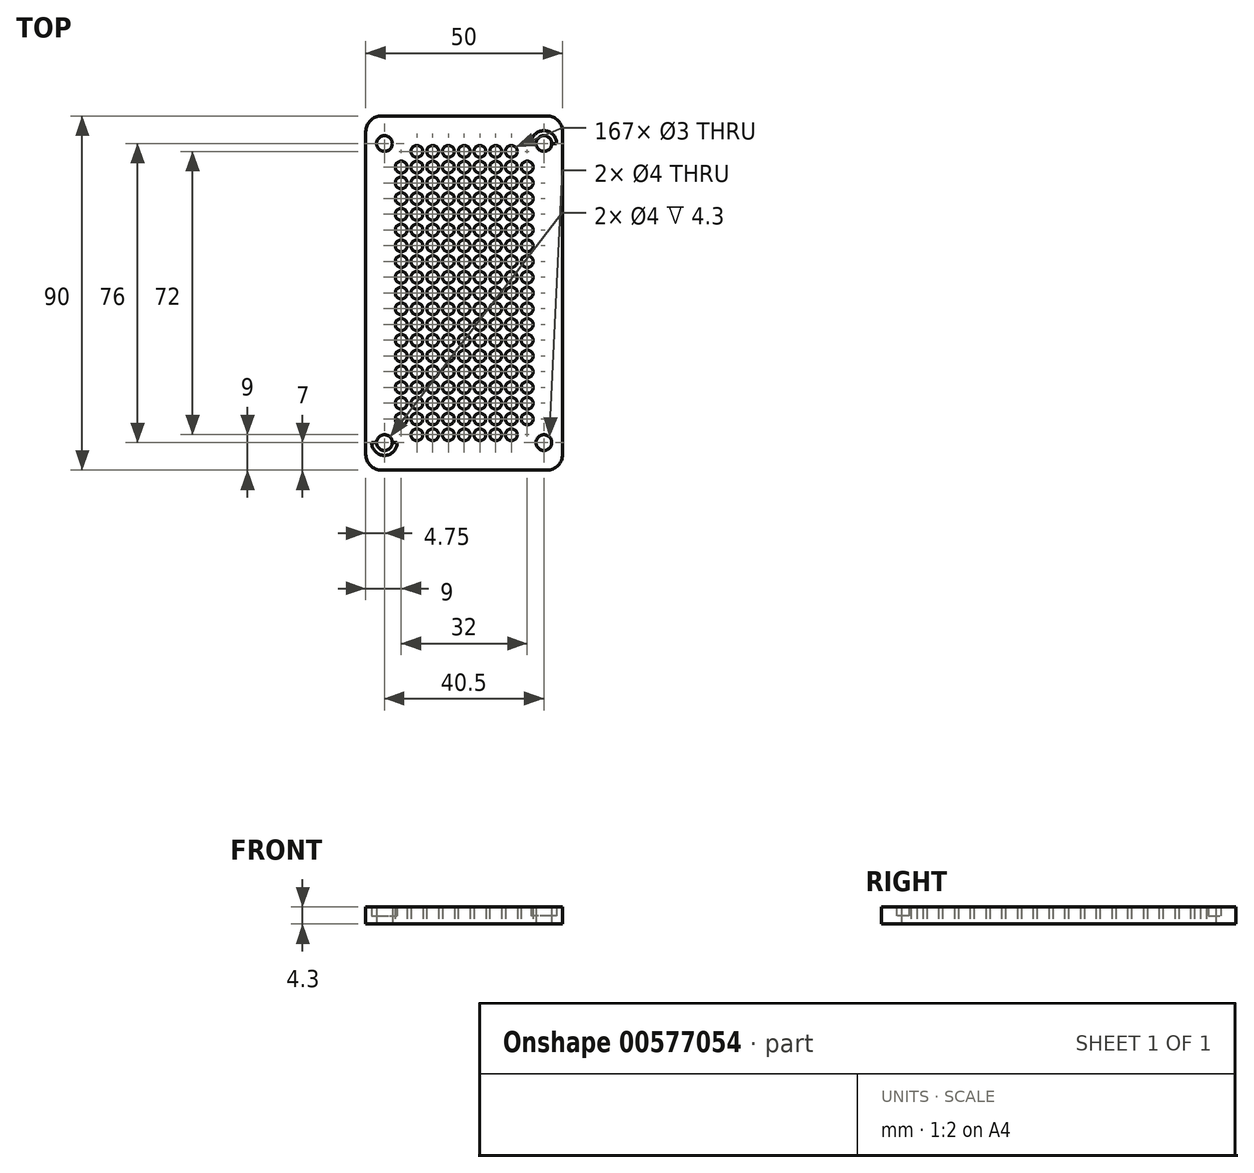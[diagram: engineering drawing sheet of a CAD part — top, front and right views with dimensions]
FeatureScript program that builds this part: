
annotation { "Feature Type Name" : "Feature", "Feature Type Description" : "" }
export const myFeature = defineFeature(function(context is Context, id is Id, definition is map)
    precondition{}
    {
        {
            var Q0;
            Q0=qCreatedBy(makeId("Top.planeOp"),FACE);
            var sketch = newSketch(context, id + "F0", { "sketchPlane" : qUnion([Q0])});
            skLineSegment(sketch, "E0.bottom", {"start": v(21, -45) * mm, "end": v(-21, -45) * mm});
            skLineSegment(sketch, "E0.top", {"start": v(21, 45) * mm, "end": v(-21, 45) * mm});
            skLineSegment(sketch, "E0.left", {"start": v(25, -41) * mm, "end": v(25, 41) * mm});
            skLineSegment(sketch, "E0.right", {"start": v(-25, -41) * mm, "end": v(-25, 41) * mm});
            skPoint(sketch, "E0.middle", {"position": v(0, 0) * mm});
            skCircle(sketch, "E1", {"center": v(0, 0) * mm, "radius": 1.5 * mm});
            skCircle(sketch, "E2.0.1.0", {"center": v(0, 4) * mm, "radius": 1.5 * mm});
            skCircle(sketch, "E2.0.2.0", {"center": v(0, 8) * mm, "radius": 1.5 * mm});
            skCircle(sketch, "E2.0.3.0", {"center": v(0, 12) * mm, "radius": 1.5 * mm});
            skCircle(sketch, "E2.0.4.0", {"center": v(0, 16) * mm, "radius": 1.5 * mm});
            skCircle(sketch, "E2.0.5.0", {"center": v(0, 20) * mm, "radius": 1.5 * mm});
            skCircle(sketch, "E2.0.6.0", {"center": v(0, 24) * mm, "radius": 1.5 * mm});
            skCircle(sketch, "E2.0.7.0", {"center": v(0, 28) * mm, "radius": 1.5 * mm});
            skCircle(sketch, "E2.0.8.0", {"center": v(0, 32) * mm, "radius": 1.5 * mm});
            skCircle(sketch, "E2.0.9.0", {"center": v(0, 36) * mm, "radius": 1.5 * mm});
            skCircle(sketch, "E2.1.0.0", {"center": v(4, 0) * mm, "radius": 1.5 * mm});
            skCircle(sketch, "E2.1.1.0", {"center": v(4, 4) * mm, "radius": 1.5 * mm});
            skCircle(sketch, "E2.1.2.0", {"center": v(4, 8) * mm, "radius": 1.5 * mm});
            skCircle(sketch, "E2.1.3.0", {"center": v(4, 12) * mm, "radius": 1.5 * mm});
            skCircle(sketch, "E2.1.4.0", {"center": v(4, 16) * mm, "radius": 1.5 * mm});
            skCircle(sketch, "E2.1.5.0", {"center": v(4, 20) * mm, "radius": 1.5 * mm});
            skCircle(sketch, "E2.1.6.0", {"center": v(4, 24) * mm, "radius": 1.5 * mm});
            skCircle(sketch, "E2.1.7.0", {"center": v(4, 28) * mm, "radius": 1.5 * mm});
            skCircle(sketch, "E2.1.8.0", {"center": v(4, 32) * mm, "radius": 1.5 * mm});
            skCircle(sketch, "E2.1.9.0", {"center": v(4, 36) * mm, "radius": 1.5 * mm});
            skCircle(sketch, "E2.2.0.0", {"center": v(8, 0) * mm, "radius": 1.5 * mm});
            skCircle(sketch, "E2.2.1.0", {"center": v(8, 4) * mm, "radius": 1.5 * mm});
            skCircle(sketch, "E2.2.2.0", {"center": v(8, 8) * mm, "radius": 1.5 * mm});
            skCircle(sketch, "E2.2.3.0", {"center": v(8, 12) * mm, "radius": 1.5 * mm});
            skCircle(sketch, "E2.2.4.0", {"center": v(8, 16) * mm, "radius": 1.5 * mm});
            skCircle(sketch, "E2.2.5.0", {"center": v(8, 20) * mm, "radius": 1.5 * mm});
            skCircle(sketch, "E2.2.6.0", {"center": v(8, 24) * mm, "radius": 1.5 * mm});
            skCircle(sketch, "E2.2.7.0", {"center": v(8, 28) * mm, "radius": 1.5 * mm});
            skCircle(sketch, "E2.2.8.0", {"center": v(8, 32) * mm, "radius": 1.5 * mm});
            skCircle(sketch, "E2.2.9.0", {"center": v(8, 36) * mm, "radius": 1.5 * mm});
            skCircle(sketch, "E2.3.0.0", {"center": v(12, 0) * mm, "radius": 1.5 * mm});
            skCircle(sketch, "E2.3.1.0", {"center": v(12, 4) * mm, "radius": 1.5 * mm});
            skCircle(sketch, "E2.3.2.0", {"center": v(12, 8) * mm, "radius": 1.5 * mm});
            skCircle(sketch, "E2.3.3.0", {"center": v(12, 12) * mm, "radius": 1.5 * mm});
            skCircle(sketch, "E2.3.4.0", {"center": v(12, 16) * mm, "radius": 1.5 * mm});
            skCircle(sketch, "E2.3.5.0", {"center": v(12, 20) * mm, "radius": 1.5 * mm});
            skCircle(sketch, "E2.3.6.0", {"center": v(12, 24) * mm, "radius": 1.5 * mm});
            skCircle(sketch, "E2.3.7.0", {"center": v(12, 28) * mm, "radius": 1.5 * mm});
            skCircle(sketch, "E2.3.8.0", {"center": v(12, 32) * mm, "radius": 1.5 * mm});
            skCircle(sketch, "E2.3.9.0", {"center": v(12, 36) * mm, "radius": 1.5 * mm});
            skCircle(sketch, "E2.4.0.0", {"center": v(16, 0) * mm, "radius": 1.5 * mm});
            skCircle(sketch, "E2.4.1.0", {"center": v(16, 4) * mm, "radius": 1.5 * mm});
            skCircle(sketch, "E2.4.2.0", {"center": v(16, 8) * mm, "radius": 1.5 * mm});
            skCircle(sketch, "E2.4.3.0", {"center": v(16, 12) * mm, "radius": 1.5 * mm});
            skCircle(sketch, "E2.4.4.0", {"center": v(16, 16) * mm, "radius": 1.5 * mm});
            skCircle(sketch, "E2.4.5.0", {"center": v(16, 20) * mm, "radius": 1.5 * mm});
            skCircle(sketch, "E2.4.6.0", {"center": v(16, 24) * mm, "radius": 1.5 * mm});
            skCircle(sketch, "E2.4.7.0", {"center": v(16, 28) * mm, "radius": 1.5 * mm});
            skCircle(sketch, "E2.4.8.0", {"center": v(16, 32) * mm, "radius": 1.5 * mm});
            skLineSegment(sketch, "E2.direction1", {"start": v(0, 0) * mm, "end": v(4, 0) * mm, "construction": true});
            skLineSegment(sketch, "E2.direction2", {"start": v(0, 0) * mm, "end": v(0, 4) * mm, "construction": true});
            skCircle(sketch, "E3.MirrorC", {"center": v(-12, 0) * mm, "radius": 1.5 * mm});
            skCircle(sketch, "E4.MirrorC", {"center": v(-16, 24) * mm, "radius": 1.5 * mm});
            skCircle(sketch, "E5.MirrorC", {"center": v(-8, 28) * mm, "radius": 1.5 * mm});
            skCircle(sketch, "E6.MirrorC", {"center": v(-12, 16) * mm, "radius": 1.5 * mm});
            skCircle(sketch, "E7.MirrorC", {"center": v(-16, 12) * mm, "radius": 1.5 * mm});
            skCircle(sketch, "E8.MirrorC", {"center": v(-8, 4) * mm, "radius": 1.5 * mm});
            skCircle(sketch, "E9.MirrorC", {"center": v(-12, 28) * mm, "radius": 1.5 * mm});
            skCircle(sketch, "E10.MirrorC", {"center": v(-8, 36) * mm, "radius": 1.5 * mm});
            skCircle(sketch, "E11.MirrorC", {"center": v(-16, 20) * mm, "radius": 1.5 * mm});
            skCircle(sketch, "E12.MirrorC", {"center": v(-8, 24) * mm, "radius": 1.5 * mm});
            skCircle(sketch, "E13.MirrorC", {"center": v(-12, 12) * mm, "radius": 1.5 * mm});
            skCircle(sketch, "E14.MirrorC", {"center": v(-16, 8) * mm, "radius": 1.5 * mm});
            skCircle(sketch, "E15.MirrorC", {"center": v(-8, 0) * mm, "radius": 1.5 * mm});
            skCircle(sketch, "E16.MirrorC", {"center": v(-12, 24) * mm, "radius": 1.5 * mm});
            skCircle(sketch, "E17.MirrorC", {"center": v(-8, 16) * mm, "radius": 1.5 * mm});
            skCircle(sketch, "E18.MirrorC", {"center": v(-16, 0) * mm, "radius": 1.5 * mm});
            skCircle(sketch, "E19.MirrorC", {"center": v(-8, 32) * mm, "radius": 1.5 * mm});
            skCircle(sketch, "E20.MirrorC", {"center": v(-16, 16) * mm, "radius": 1.5 * mm});
            skCircle(sketch, "E21.MirrorC", {"center": v(-12, 8) * mm, "radius": 1.5 * mm});
            skCircle(sketch, "E22.MirrorC", {"center": v(-8, 20) * mm, "radius": 1.5 * mm});
            skCircle(sketch, "E23.MirrorC", {"center": v(-16, 32) * mm, "radius": 1.5 * mm});
            skCircle(sketch, "E24.MirrorC", {"center": v(-16, 4) * mm, "radius": 1.5 * mm});
            skCircle(sketch, "E25.MirrorC", {"center": v(-12, 20) * mm, "radius": 1.5 * mm});
            skCircle(sketch, "E26.MirrorC", {"center": v(-8, 12) * mm, "radius": 1.5 * mm});
            skCircle(sketch, "E27.MirrorC", {"center": v(-12, 36) * mm, "radius": 1.5 * mm});
            skCircle(sketch, "E28.MirrorC", {"center": v(-12, 4) * mm, "radius": 1.5 * mm});
            skCircle(sketch, "E29.MirrorC", {"center": v(-16, 28) * mm, "radius": 1.5 * mm});
            skCircle(sketch, "E30.MirrorC", {"center": v(-8, 8) * mm, "radius": 1.5 * mm});
            skCircle(sketch, "E31.MirrorC", {"center": v(-12, 32) * mm, "radius": 1.5 * mm});
            skCircle(sketch, "E32.MirrorC", {"center": v(-4, 16) * mm, "radius": 1.5 * mm});
            skCircle(sketch, "E33.MirrorC", {"center": v(-4, 12) * mm, "radius": 1.5 * mm});
            skCircle(sketch, "E34.MirrorC", {"center": v(-4, 8) * mm, "radius": 1.5 * mm});
            skCircle(sketch, "E35.MirrorC", {"center": v(-4, 36) * mm, "radius": 1.5 * mm});
            skCircle(sketch, "E36.MirrorC", {"center": v(-4, 20) * mm, "radius": 1.5 * mm});
            skCircle(sketch, "E37.MirrorC", {"center": v(-4, 32) * mm, "radius": 1.5 * mm});
            skCircle(sketch, "E38.MirrorC", {"center": v(-4, 0) * mm, "radius": 1.5 * mm});
            skCircle(sketch, "E39.MirrorC", {"center": v(-4, 4) * mm, "radius": 1.5 * mm});
            skCircle(sketch, "E40.MirrorC", {"center": v(-4, 24) * mm, "radius": 1.5 * mm});
            skCircle(sketch, "E41.MirrorC", {"center": v(-4, 28) * mm, "radius": 1.5 * mm});
            skCircle(sketch, "E42.MirrorC", {"center": v(16, -24) * mm, "radius": 1.5 * mm});
            skCircle(sketch, "E43.MirrorC", {"center": v(-12, -12) * mm, "radius": 1.5 * mm});
            skCircle(sketch, "E44.MirrorC", {"center": v(-12, -4) * mm, "radius": 1.5 * mm});
            skCircle(sketch, "E45.MirrorC", {"center": v(4, -16) * mm, "radius": 1.5 * mm});
            skCircle(sketch, "E46.MirrorC", {"center": v(-8, -32) * mm, "radius": 1.5 * mm});
            skCircle(sketch, "E47.MirrorC", {"center": v(-4, -36) * mm, "radius": 1.5 * mm});
            skCircle(sketch, "E48.MirrorC", {"center": v(8, -4) * mm, "radius": 1.5 * mm});
            skCircle(sketch, "E49.MirrorC", {"center": v(12, -28) * mm, "radius": 1.5 * mm});
            skCircle(sketch, "E50.MirrorC", {"center": v(-16, -24) * mm, "radius": 1.5 * mm});
            skCircle(sketch, "E51.MirrorC", {"center": v(-8, -28) * mm, "radius": 1.5 * mm});
            skCircle(sketch, "E52.MirrorC", {"center": v(12, -32) * mm, "radius": 1.5 * mm});
            skCircle(sketch, "E53.MirrorC", {"center": v(8, -8) * mm, "radius": 1.5 * mm});
            skCircle(sketch, "E54.MirrorC", {"center": v(-4, -20) * mm, "radius": 1.5 * mm});
            skCircle(sketch, "E55.MirrorC", {"center": v(-16, -16) * mm, "radius": 1.5 * mm});
            skCircle(sketch, "E56.MirrorC", {"center": v(4, -20) * mm, "radius": 1.5 * mm});
            skCircle(sketch, "E57.MirrorC", {"center": v(-16, -28) * mm, "radius": 1.5 * mm});
            skCircle(sketch, "E58.MirrorC", {"center": v(16, -28) * mm, "radius": 1.5 * mm});
            skCircle(sketch, "E59.MirrorC", {"center": v(12, -4) * mm, "radius": 1.5 * mm});
            skCircle(sketch, "E60.MirrorC", {"center": v(-12, -16) * mm, "radius": 1.5 * mm});
            skCircle(sketch, "E61.MirrorC", {"center": v(12, -36) * mm, "radius": 1.5 * mm});
            skCircle(sketch, "E62.MirrorC", {"center": v(8, -12) * mm, "radius": 1.5 * mm});
            skCircle(sketch, "E63.MirrorC", {"center": v(-4, -32) * mm, "radius": 1.5 * mm});
            skCircle(sketch, "E64.MirrorC", {"center": v(-12, -8) * mm, "radius": 1.5 * mm});
            skCircle(sketch, "E65.MirrorC", {"center": v(4, -24) * mm, "radius": 1.5 * mm});
            skCircle(sketch, "E66.MirrorC", {"center": v(-8, -8) * mm, "radius": 1.5 * mm});
            skCircle(sketch, "E67.MirrorC", {"center": v(-8, -4) * mm, "radius": 1.5 * mm});
            skCircle(sketch, "E68.MirrorC", {"center": v(-16, -32) * mm, "radius": 1.5 * mm});
            skCircle(sketch, "E69.MirrorC", {"center": v(-16, -8) * mm, "radius": 1.5 * mm});
            skCircle(sketch, "E70.MirrorC", {"center": v(16, -4) * mm, "radius": 1.5 * mm});
            skCircle(sketch, "E71.MirrorC", {"center": v(12, -8) * mm, "radius": 1.5 * mm});
            skCircle(sketch, "E72.MirrorC", {"center": v(16, -32) * mm, "radius": 1.5 * mm});
            skCircle(sketch, "E73.MirrorC", {"center": v(8, -20) * mm, "radius": 1.5 * mm});
            skCircle(sketch, "E74.MirrorC", {"center": v(-4, -4) * mm, "radius": 1.5 * mm});
            skCircle(sketch, "E75.MirrorC", {"center": v(8, -36) * mm, "radius": 1.5 * mm});
            skCircle(sketch, "E76.MirrorC", {"center": v(16, -20) * mm, "radius": 1.5 * mm});
            skCircle(sketch, "E77.MirrorC", {"center": v(-8, -24) * mm, "radius": 1.5 * mm});
            skCircle(sketch, "E78.MirrorC", {"center": v(-12, -36) * mm, "radius": 1.5 * mm});
            skCircle(sketch, "E79.MirrorC", {"center": v(4, -12) * mm, "radius": 1.5 * mm});
            skCircle(sketch, "E80.MirrorC", {"center": v(-4, -8) * mm, "radius": 1.5 * mm});
            skCircle(sketch, "E81.MirrorC", {"center": v(12, -24) * mm, "radius": 1.5 * mm});
            skCircle(sketch, "E82.MirrorC", {"center": v(4, -4) * mm, "radius": 1.5 * mm});
            skCircle(sketch, "E83.MirrorC", {"center": v(0, -36) * mm, "radius": 1.5 * mm});
            skCircle(sketch, "E84.MirrorC", {"center": v(-4, -28) * mm, "radius": 1.5 * mm});
            skCircle(sketch, "E85.MirrorC", {"center": v(12, -16) * mm, "radius": 1.5 * mm});
            skCircle(sketch, "E86.MirrorC", {"center": v(8, -28) * mm, "radius": 1.5 * mm});
            skCircle(sketch, "E87.MirrorC", {"center": v(-8, -36) * mm, "radius": 1.5 * mm});
            skCircle(sketch, "E88.MirrorC", {"center": v(-12, -24) * mm, "radius": 1.5 * mm});
            skCircle(sketch, "E89.MirrorC", {"center": v(16, -12) * mm, "radius": 1.5 * mm});
            skCircle(sketch, "E90.MirrorC", {"center": v(-12, -20) * mm, "radius": 1.5 * mm});
            skCircle(sketch, "E91.MirrorC", {"center": v(-4, -16) * mm, "radius": 1.5 * mm});
            skCircle(sketch, "E92.MirrorC", {"center": v(4, -32) * mm, "radius": 1.5 * mm});
            skCircle(sketch, "E93.MirrorC", {"center": v(8, -32) * mm, "radius": 1.5 * mm});
            skCircle(sketch, "E94.MirrorC", {"center": v(16, -16) * mm, "radius": 1.5 * mm});
            skCircle(sketch, "E95.MirrorC", {"center": v(-4, -24) * mm, "radius": 1.5 * mm});
            skCircle(sketch, "E96.MirrorC", {"center": v(12, -12) * mm, "radius": 1.5 * mm});
            skCircle(sketch, "E97.MirrorC", {"center": v(8, -24) * mm, "radius": 1.5 * mm});
            skCircle(sketch, "E98.MirrorC", {"center": v(-16, -20) * mm, "radius": 1.5 * mm});
            skCircle(sketch, "E99.MirrorC", {"center": v(-8, -12) * mm, "radius": 1.5 * mm});
            skCircle(sketch, "E100.MirrorC", {"center": v(4, -8) * mm, "radius": 1.5 * mm});
            skCircle(sketch, "E101.MirrorC", {"center": v(-8, -16) * mm, "radius": 1.5 * mm});
            skCircle(sketch, "E102.MirrorC", {"center": v(-4, -12) * mm, "radius": 1.5 * mm});
            skCircle(sketch, "E103.MirrorC", {"center": v(12, -20) * mm, "radius": 1.5 * mm});
            skCircle(sketch, "E104.MirrorC", {"center": v(4, -36) * mm, "radius": 1.5 * mm});
            skCircle(sketch, "E105.MirrorC", {"center": v(0, -32) * mm, "radius": 1.5 * mm});
            skCircle(sketch, "E106.MirrorC", {"center": v(0, -28) * mm, "radius": 1.5 * mm});
            skCircle(sketch, "E107.MirrorC", {"center": v(0, -24) * mm, "radius": 1.5 * mm});
            skCircle(sketch, "E108.MirrorC", {"center": v(0, -20) * mm, "radius": 1.5 * mm});
            skCircle(sketch, "E109.MirrorC", {"center": v(0, -16) * mm, "radius": 1.5 * mm});
            skCircle(sketch, "E110.MirrorC", {"center": v(0, -12) * mm, "radius": 1.5 * mm});
            skCircle(sketch, "E111.MirrorC", {"center": v(0, -8) * mm, "radius": 1.5 * mm});
            skCircle(sketch, "E112.MirrorC", {"center": v(16, -8) * mm, "radius": 1.5 * mm});
            skCircle(sketch, "E113.MirrorC", {"center": v(-12, -28) * mm, "radius": 1.5 * mm});
            skCircle(sketch, "E114.MirrorC", {"center": v(-12, -32) * mm, "radius": 1.5 * mm});
            skCircle(sketch, "E115.MirrorC", {"center": v(-16, -4) * mm, "radius": 1.5 * mm});
            skCircle(sketch, "E116.MirrorC", {"center": v(4, -28) * mm, "radius": 1.5 * mm});
            skCircle(sketch, "E117.MirrorC", {"center": v(-8, -20) * mm, "radius": 1.5 * mm});
            skCircle(sketch, "E118.MirrorC", {"center": v(-16, -12) * mm, "radius": 1.5 * mm});
            skCircle(sketch, "E119.MirrorC", {"center": v(8, -16) * mm, "radius": 1.5 * mm});
            skCircle(sketch, "E120.MirrorC", {"center": v(0, -4) * mm, "radius": 1.5 * mm});
            skPoint(sketch, "E121.visualSharp", {"position": v(-25, 45) * mm});
            skArc(sketch, "E121.filletArc", {"start": v(-21, 45) * mm, "mid": v(-23.83, 43.83) * mm, "end": v(-25, 41) * mm});
            skPoint(sketch, "E122.visualSharp", {"position": v(25, 45) * mm});
            skArc(sketch, "E122.filletArc", {"start": v(25, 41) * mm, "mid": v(23.83, 43.83) * mm, "end": v(21, 45) * mm});
            skPoint(sketch, "E123.visualSharp", {"position": v(-25, -45) * mm});
            skArc(sketch, "E123.filletArc", {"start": v(-25, -41) * mm, "mid": v(-23.83, -43.83) * mm, "end": v(-21, -45) * mm});
            skPoint(sketch, "E124.visualSharp", {"position": v(25, -45) * mm});
            skArc(sketch, "E124.filletArc", {"start": v(21, -45) * mm, "mid": v(23.83, -43.83) * mm, "end": v(25, -41) * mm});
            skCircle(sketch, "E125", {"center": v(-20.25, 38) * mm, "radius": 2 * mm});
            skCircle(sketch, "E126.MirrorC", {"center": v(20.25, 38) * mm, "radius": 2 * mm});
            skCircle(sketch, "E127.MirrorC", {"center": v(-20.25, -38) * mm, "radius": 2 * mm});
            skCircle(sketch, "E128.MirrorC", {"center": v(20.25, -38) * mm, "radius": 2 * mm});
            skSolve(sketch);
        }
        {
            var Q0;
            Q0=makeQuery(id+"F0.imprint","IMPRINT",FACE,{"disambiguationData":[TD([[makeQuery(id+"F0.imprint","IMPRINT",EDGE,{"derivedFrom":sQuery(id+"F0.wireOp",EDGE,"E0.bottom")}),-1.0]])]});
            extrude(context, id + "F1", {"entities" : qUnion([Q0]), "depth" : 2 * mm, "offsetDistance" : 25 * mm});
        }
        {
            var Q0;
            Q0=makeQuery(id+"F1.opExtrude","CAP_FACE",FACE,{"disambiguationData":[OSD([sQuery(id+"F0.wireOp",EDGE,"E0.bottom"),sQuery(id+"F0.wireOp",EDGE,"E0.top"),sQuery(id+"F0.wireOp",EDGE,"E0.left"),sQuery(id+"F0.wireOp",EDGE,"E0.right"),sQuery(id+"F0.wireOp",EDGE,"E1"),sQuery(id+"F0.wireOp",EDGE,"E2.0.1.0"),sQuery(id+"F0.wireOp",EDGE,"E2.0.2.0"),sQuery(id+"F0.wireOp",EDGE,"E2.0.3.0"),sQuery(id+"F0.wireOp",EDGE,"E2.0.4.0"),sQuery(id+"F0.wireOp",EDGE,"E2.0.5.0"),sQuery(id+"F0.wireOp",EDGE,"E2.0.6.0"),sQuery(id+"F0.wireOp",EDGE,"E2.0.7.0"),sQuery(id+"F0.wireOp",EDGE,"E2.0.8.0"),sQuery(id+"F0.wireOp",EDGE,"E2.0.9.0"),sQuery(id+"F0.wireOp",EDGE,"E2.1.0.0"),sQuery(id+"F0.wireOp",EDGE,"E2.1.1.0"),sQuery(id+"F0.wireOp",EDGE,"E2.1.2.0"),sQuery(id+"F0.wireOp",EDGE,"E2.1.3.0"),sQuery(id+"F0.wireOp",EDGE,"E2.1.4.0"),sQuery(id+"F0.wireOp",EDGE,"E2.1.5.0"),sQuery(id+"F0.wireOp",EDGE,"E2.1.6.0"),sQuery(id+"F0.wireOp",EDGE,"E2.1.7.0"),sQuery(id+"F0.wireOp",EDGE,"E2.1.8.0"),sQuery(id+"F0.wireOp",EDGE,"E2.1.9.0"),sQuery(id+"F0.wireOp",EDGE,"E2.2.0.0"),sQuery(id+"F0.wireOp",EDGE,"E2.2.1.0"),sQuery(id+"F0.wireOp",EDGE,"E2.2.2.0"),sQuery(id+"F0.wireOp",EDGE,"E2.2.3.0"),sQuery(id+"F0.wireOp",EDGE,"E2.2.4.0"),sQuery(id+"F0.wireOp",EDGE,"E2.2.5.0"),sQuery(id+"F0.wireOp",EDGE,"E2.2.6.0"),sQuery(id+"F0.wireOp",EDGE,"E2.2.7.0"),sQuery(id+"F0.wireOp",EDGE,"E2.2.8.0"),sQuery(id+"F0.wireOp",EDGE,"E2.2.9.0"),sQuery(id+"F0.wireOp",EDGE,"E2.3.0.0"),sQuery(id+"F0.wireOp",EDGE,"E2.3.1.0"),sQuery(id+"F0.wireOp",EDGE,"E2.3.2.0"),sQuery(id+"F0.wireOp",EDGE,"E2.3.3.0"),sQuery(id+"F0.wireOp",EDGE,"E2.3.4.0"),sQuery(id+"F0.wireOp",EDGE,"E2.3.5.0"),sQuery(id+"F0.wireOp",EDGE,"E2.3.6.0"),sQuery(id+"F0.wireOp",EDGE,"E2.3.7.0"),sQuery(id+"F0.wireOp",EDGE,"E2.3.8.0"),sQuery(id+"F0.wireOp",EDGE,"E2.3.9.0"),sQuery(id+"F0.wireOp",EDGE,"E2.4.0.0"),sQuery(id+"F0.wireOp",EDGE,"E2.4.1.0"),sQuery(id+"F0.wireOp",EDGE,"E2.4.2.0"),sQuery(id+"F0.wireOp",EDGE,"E2.4.3.0"),sQuery(id+"F0.wireOp",EDGE,"E2.4.4.0"),sQuery(id+"F0.wireOp",EDGE,"E2.4.5.0"),sQuery(id+"F0.wireOp",EDGE,"E2.4.6.0"),sQuery(id+"F0.wireOp",EDGE,"E2.4.7.0"),sQuery(id+"F0.wireOp",EDGE,"E2.4.8.0"),sQuery(id+"F0.wireOp",EDGE,"E3.MirrorC"),sQuery(id+"F0.wireOp",EDGE,"E4.MirrorC"),sQuery(id+"F0.wireOp",EDGE,"E5.MirrorC"),sQuery(id+"F0.wireOp",EDGE,"E6.MirrorC"),sQuery(id+"F0.wireOp",EDGE,"E7.MirrorC"),sQuery(id+"F0.wireOp",EDGE,"E8.MirrorC"),sQuery(id+"F0.wireOp",EDGE,"E9.MirrorC"),sQuery(id+"F0.wireOp",EDGE,"E10.MirrorC"),sQuery(id+"F0.wireOp",EDGE,"E11.MirrorC"),sQuery(id+"F0.wireOp",EDGE,"E12.MirrorC"),sQuery(id+"F0.wireOp",EDGE,"E13.MirrorC"),sQuery(id+"F0.wireOp",EDGE,"E14.MirrorC"),sQuery(id+"F0.wireOp",EDGE,"E15.MirrorC"),sQuery(id+"F0.wireOp",EDGE,"E16.MirrorC"),sQuery(id+"F0.wireOp",EDGE,"E17.MirrorC"),sQuery(id+"F0.wireOp",EDGE,"E18.MirrorC"),sQuery(id+"F0.wireOp",EDGE,"E19.MirrorC"),sQuery(id+"F0.wireOp",EDGE,"E20.MirrorC"),sQuery(id+"F0.wireOp",EDGE,"E21.MirrorC"),sQuery(id+"F0.wireOp",EDGE,"E22.MirrorC"),sQuery(id+"F0.wireOp",EDGE,"E23.MirrorC"),sQuery(id+"F0.wireOp",EDGE,"E24.MirrorC"),sQuery(id+"F0.wireOp",EDGE,"E25.MirrorC"),sQuery(id+"F0.wireOp",EDGE,"E26.MirrorC"),sQuery(id+"F0.wireOp",EDGE,"E27.MirrorC"),sQuery(id+"F0.wireOp",EDGE,"E28.MirrorC"),sQuery(id+"F0.wireOp",EDGE,"E29.MirrorC"),sQuery(id+"F0.wireOp",EDGE,"E30.MirrorC"),sQuery(id+"F0.wireOp",EDGE,"E31.MirrorC"),sQuery(id+"F0.wireOp",EDGE,"E32.MirrorC"),sQuery(id+"F0.wireOp",EDGE,"E33.MirrorC"),sQuery(id+"F0.wireOp",EDGE,"E34.MirrorC"),sQuery(id+"F0.wireOp",EDGE,"E35.MirrorC"),sQuery(id+"F0.wireOp",EDGE,"E36.MirrorC"),sQuery(id+"F0.wireOp",EDGE,"E37.MirrorC"),sQuery(id+"F0.wireOp",EDGE,"E38.MirrorC"),sQuery(id+"F0.wireOp",EDGE,"E39.MirrorC"),sQuery(id+"F0.wireOp",EDGE,"E40.MirrorC"),sQuery(id+"F0.wireOp",EDGE,"E41.MirrorC"),sQuery(id+"F0.wireOp",EDGE,"E42.MirrorC"),sQuery(id+"F0.wireOp",EDGE,"E43.MirrorC"),sQuery(id+"F0.wireOp",EDGE,"E44.MirrorC"),sQuery(id+"F0.wireOp",EDGE,"E45.MirrorC"),sQuery(id+"F0.wireOp",EDGE,"E46.MirrorC"),sQuery(id+"F0.wireOp",EDGE,"E47.MirrorC"),sQuery(id+"F0.wireOp",EDGE,"E48.MirrorC"),sQuery(id+"F0.wireOp",EDGE,"E49.MirrorC"),sQuery(id+"F0.wireOp",EDGE,"E50.MirrorC"),sQuery(id+"F0.wireOp",EDGE,"E51.MirrorC"),sQuery(id+"F0.wireOp",EDGE,"E52.MirrorC"),sQuery(id+"F0.wireOp",EDGE,"E53.MirrorC"),sQuery(id+"F0.wireOp",EDGE,"E54.MirrorC"),sQuery(id+"F0.wireOp",EDGE,"E55.MirrorC"),sQuery(id+"F0.wireOp",EDGE,"E56.MirrorC"),sQuery(id+"F0.wireOp",EDGE,"E57.MirrorC"),sQuery(id+"F0.wireOp",EDGE,"E58.MirrorC"),sQuery(id+"F0.wireOp",EDGE,"E59.MirrorC"),sQuery(id+"F0.wireOp",EDGE,"E60.MirrorC"),sQuery(id+"F0.wireOp",EDGE,"E61.MirrorC"),sQuery(id+"F0.wireOp",EDGE,"E62.MirrorC"),sQuery(id+"F0.wireOp",EDGE,"E63.MirrorC"),sQuery(id+"F0.wireOp",EDGE,"E64.MirrorC"),sQuery(id+"F0.wireOp",EDGE,"E65.MirrorC"),sQuery(id+"F0.wireOp",EDGE,"E66.MirrorC"),sQuery(id+"F0.wireOp",EDGE,"E67.MirrorC"),sQuery(id+"F0.wireOp",EDGE,"E68.MirrorC"),sQuery(id+"F0.wireOp",EDGE,"E69.MirrorC"),sQuery(id+"F0.wireOp",EDGE,"E70.MirrorC"),sQuery(id+"F0.wireOp",EDGE,"E71.MirrorC"),sQuery(id+"F0.wireOp",EDGE,"E72.MirrorC"),sQuery(id+"F0.wireOp",EDGE,"E73.MirrorC"),sQuery(id+"F0.wireOp",EDGE,"E74.MirrorC"),sQuery(id+"F0.wireOp",EDGE,"E75.MirrorC"),sQuery(id+"F0.wireOp",EDGE,"E76.MirrorC"),sQuery(id+"F0.wireOp",EDGE,"E77.MirrorC"),sQuery(id+"F0.wireOp",EDGE,"E78.MirrorC"),sQuery(id+"F0.wireOp",EDGE,"E79.MirrorC"),sQuery(id+"F0.wireOp",EDGE,"E80.MirrorC"),sQuery(id+"F0.wireOp",EDGE,"E81.MirrorC"),sQuery(id+"F0.wireOp",EDGE,"E82.MirrorC"),sQuery(id+"F0.wireOp",EDGE,"E83.MirrorC"),sQuery(id+"F0.wireOp",EDGE,"E84.MirrorC"),sQuery(id+"F0.wireOp",EDGE,"E85.MirrorC"),sQuery(id+"F0.wireOp",EDGE,"E86.MirrorC"),sQuery(id+"F0.wireOp",EDGE,"E87.MirrorC"),sQuery(id+"F0.wireOp",EDGE,"E88.MirrorC"),sQuery(id+"F0.wireOp",EDGE,"E89.MirrorC"),sQuery(id+"F0.wireOp",EDGE,"E90.MirrorC"),sQuery(id+"F0.wireOp",EDGE,"E91.MirrorC"),sQuery(id+"F0.wireOp",EDGE,"E92.MirrorC"),sQuery(id+"F0.wireOp",EDGE,"E93.MirrorC"),sQuery(id+"F0.wireOp",EDGE,"E94.MirrorC"),sQuery(id+"F0.wireOp",EDGE,"E95.MirrorC"),sQuery(id+"F0.wireOp",EDGE,"E96.MirrorC"),sQuery(id+"F0.wireOp",EDGE,"E97.MirrorC"),sQuery(id+"F0.wireOp",EDGE,"E98.MirrorC"),sQuery(id+"F0.wireOp",EDGE,"E99.MirrorC"),sQuery(id+"F0.wireOp",EDGE,"E100.MirrorC"),sQuery(id+"F0.wireOp",EDGE,"E101.MirrorC"),sQuery(id+"F0.wireOp",EDGE,"E102.MirrorC"),sQuery(id+"F0.wireOp",EDGE,"E103.MirrorC"),sQuery(id+"F0.wireOp",EDGE,"E104.MirrorC"),sQuery(id+"F0.wireOp",EDGE,"E105.MirrorC"),sQuery(id+"F0.wireOp",EDGE,"E106.MirrorC"),sQuery(id+"F0.wireOp",EDGE,"E107.MirrorC"),sQuery(id+"F0.wireOp",EDGE,"E108.MirrorC"),sQuery(id+"F0.wireOp",EDGE,"E109.MirrorC"),sQuery(id+"F0.wireOp",EDGE,"E110.MirrorC"),sQuery(id+"F0.wireOp",EDGE,"E111.MirrorC"),sQuery(id+"F0.wireOp",EDGE,"E112.MirrorC"),sQuery(id+"F0.wireOp",EDGE,"E113.MirrorC"),sQuery(id+"F0.wireOp",EDGE,"E114.MirrorC"),sQuery(id+"F0.wireOp",EDGE,"E115.MirrorC"),sQuery(id+"F0.wireOp",EDGE,"E116.MirrorC"),sQuery(id+"F0.wireOp",EDGE,"E117.MirrorC"),sQuery(id+"F0.wireOp",EDGE,"E118.MirrorC"),sQuery(id+"F0.wireOp",EDGE,"E119.MirrorC"),sQuery(id+"F0.wireOp",EDGE,"E120.MirrorC"),sQuery(id+"F0.wireOp",EDGE,"E121.filletArc"),sQuery(id+"F0.wireOp",EDGE,"E122.filletArc"),sQuery(id+"F0.wireOp",EDGE,"E123.filletArc"),sQuery(id+"F0.wireOp",EDGE,"E124.filletArc"),sQuery(id+"F0.wireOp",EDGE,"E125"),sQuery(id+"F0.wireOp",EDGE,"E126.MirrorC"),sQuery(id+"F0.wireOp",EDGE,"E127.MirrorC"),sQuery(id+"F0.wireOp",EDGE,"E128.MirrorC")])],"isStart":false});
            var sketch = newSketch(context, id + "F2", { "sketchPlane" : qUnion([Q0])});
            skPoint(sketch, "E129.0", {"position": v(-20.25, 38) * mm});
            skPoint(sketch, "E130.0", {"position": v(20.25, 38) * mm});
            skPoint(sketch, "E131.0", {"position": v(20.25, -38) * mm});
            skPoint(sketch, "E132.0", {"position": v(-20.25, -38) * mm});
            skLineSegment(sketch, "E133", {"start": v(-20.25, 38) * mm, "end": v(-20.25, 40) * mm, "construction": true});
            skLineSegment(sketch, "E134", {"start": v(-22.25, 38) * mm, "end": v(-18.25, 38) * mm, "construction": true});
            skArc(sketch, "E135", {"start": v(-18.25, 38) * mm, "mid": v(-20.25, 40) * mm, "end": v(-22.25, 38) * mm});
            skArc(sketch, "E136.0", {"start": v(-17, 38) * mm, "mid": v(-20.25, 41.25) * mm, "end": v(-23.5, 38) * mm});
            skLineSegment(sketch, "E137", {"start": v(-23.5, 38) * mm, "end": v(-22.25, 38) * mm});
            skLineSegment(sketch, "E138", {"start": v(-18.25, 38) * mm, "end": v(-17, 38) * mm});
            skArc(sketch, "E139.MirrorCS", {"start": v(17, 38) * mm, "mid": v(20.25, 41.25) * mm, "end": v(23.5, 38) * mm});
            skArc(sketch, "E140.MirrorCS", {"start": v(18.25, 38) * mm, "mid": v(20.25, 40) * mm, "end": v(22.25, 38) * mm});
            skLineSegment(sketch, "E141.MirrorCS", {"start": v(23.5, 38) * mm, "end": v(22.25, 38) * mm});
            skLineSegment(sketch, "E142.MirrorCS", {"start": v(18.25, 38) * mm, "end": v(17, 38) * mm});
            skArc(sketch, "E143.MirrorCS", {"start": v(-17, -38) * mm, "mid": v(-20.25, -41.25) * mm, "end": v(-23.5, -38) * mm});
            skLineSegment(sketch, "E144.MirrorCS", {"start": v(-23.5, -38) * mm, "end": v(-22.25, -38) * mm});
            skArc(sketch, "E145.MirrorCS", {"start": v(-18.25, -38) * mm, "mid": v(-20.25, -40) * mm, "end": v(-22.25, -38) * mm});
            skLineSegment(sketch, "E146.MirrorCS", {"start": v(-18.25, -38) * mm, "end": v(-17, -38) * mm});
            skArc(sketch, "E147.MirrorCS", {"start": v(17, -38) * mm, "mid": v(20.25, -41.25) * mm, "end": v(23.5, -38) * mm});
            skArc(sketch, "E148.MirrorCS", {"start": v(18.25, -38) * mm, "mid": v(20.25, -40) * mm, "end": v(22.25, -38) * mm});
            skLineSegment(sketch, "E149.MirrorCS", {"start": v(18.25, -38) * mm, "end": v(17, -38) * mm});
            skLineSegment(sketch, "E150.MirrorCS", {"start": v(23.5, -38) * mm, "end": v(22.25, -38) * mm});
            skSolve(sketch);
        }
        {
            var Q0;
            Q0=makeQuery(id+"F2.imprint","IMPRINT",FACE,{"disambiguationData":[TD([[makeQuery(id+"F2.imprint","IMPRINT",EDGE,{"derivedFrom":sQuery(id+"F2.wireOp",EDGE,"E135")}),-1.0]])]});
            var Q1;
            Q1=makeQuery(id+"F2.imprint","IMPRINT",FACE,{"disambiguationData":[TD([[makeQuery(id+"F2.imprint","IMPRINT",EDGE,{"derivedFrom":sQuery(id+"F2.wireOp",EDGE,"E139.MirrorCS")}),-1.0]])]});
            var Q2;
            Q2=makeQuery(id+"F2.imprint","IMPRINT",FACE,{"disambiguationData":[TD([[makeQuery(id+"F2.imprint","IMPRINT",EDGE,{"derivedFrom":sQuery(id+"F2.wireOp",EDGE,"E147.MirrorCS")}),1.0]])]});
            var Q3;
            Q3=makeQuery(id+"F2.imprint","IMPRINT",FACE,{"disambiguationData":[TD([[makeQuery(id+"F2.imprint","IMPRINT",EDGE,{"derivedFrom":sQuery(id+"F2.wireOp",EDGE,"E143.MirrorCS")}),-1.0]])]});
            extrude(context, id + "F3", {"entities" : qUnion([Q0, Q1, Q2, Q3]), "operationType" : NewBodyOperationType.ADD, "depth" : 2.3 * mm, "offsetDistance" : 25 * mm});
        }
    });
